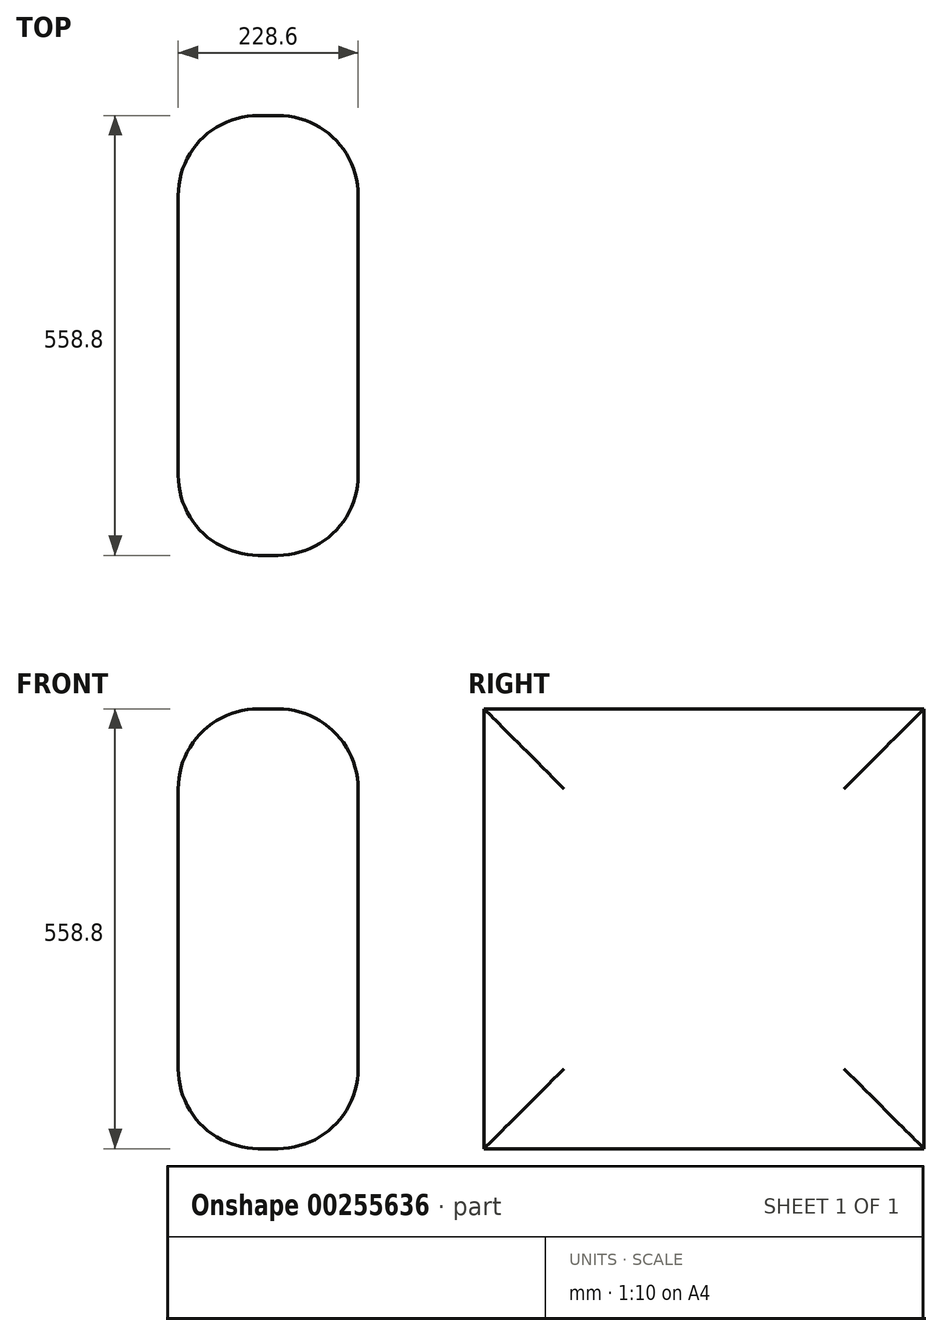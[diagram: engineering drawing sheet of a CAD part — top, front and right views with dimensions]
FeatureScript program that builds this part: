
annotation { "Feature Type Name" : "Feature", "Feature Type Description" : "" }
export const myFeature = defineFeature(function(context is Context, id is Id, definition is map)
    precondition{}
    {
        {
            var Q0;
            Q0=qCreatedBy(makeId("Top.planeOp"),FACE);
            var sketch = newSketch(context, id + "F0", { "sketchPlane" : qUnion([Q0])});
            skLineSegment(sketch, "E0.bottom", {"start": v(-253.01, 515.56) * mm, "end": v(-24.41, 515.56) * mm});
            skLineSegment(sketch, "E0.top", {"start": v(-253.01, -43.24) * mm, "end": v(-24.41, -43.24) * mm});
            skLineSegment(sketch, "E0.left", {"start": v(-253.01, 515.56) * mm, "end": v(-253.01, -43.24) * mm});
            skLineSegment(sketch, "E0.right", {"start": v(-24.41, 515.56) * mm, "end": v(-24.41, -43.24) * mm});
            skSolve(sketch);
        }
        {
            var Q0;
            Q0 = qSketchRegion(id + "F0", true);
            extrude(context, id + "F1", {"entities" : qUnion([Q0]), "depth" : 558.8 * mm});
        }
        {
            var Q0;
            Q0=makeQuery(id+"F1.opExtrude","SWEPT_FACE",FACE,{"disambiguationData":[OSD([sQuery(id+"F0.wireOp",EDGE,"E0.right")])]});
            var Q1;
            Q1=makeQuery(id+"F1.opExtrude","SWEPT_FACE",FACE,{"disambiguationData":[OSD([sQuery(id+"F0.wireOp",EDGE,"E0.left")])]});
            fillet(context, id + "F2", {"entities" : qUnion([Q0, Q1]), "radius" : 101.6 * mm, "tangentPropagation" : true, "allowEdgeOverflow" : false});
        }
    });
